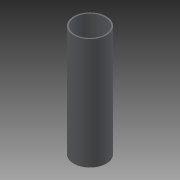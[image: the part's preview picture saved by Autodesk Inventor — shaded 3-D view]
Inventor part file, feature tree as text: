
AUTODESK INVENTOR PART (.ipt)
format: ipt  version: 2014 (Build 180170000, 170)  size: 102,912 bytes
history: native  units: in
note: dims shown in document units (in); Inventor stores cm internally (conversion verified against a paired STEP export)
features: other x14, revolve x1, sketch x1
ambient origin geometry x8: Origin, YZ Plane, XZ Plane, XY Plane, X Axis, Y Axis, Z Axis, Center Point
bodies: Solid1 (feature_tree)
feature tree (16):
  revolve  "Revolution1"  [1 undecoded]
  other  "tube_rear_XY"
  other  "tube_rear_YZ"
  other  "tube_rear_ZX"
  other  "tube_rear_X"
  other  "tube_rear_Y"
  other  "tube_rear_Z"
  other  "tube_rear_Center"
  other  "tube_rod_guide_XY"
  other  "tube_rod_guide_YZ"
  other  "tube_rod_guide_ZX"
  other  "tube_rod_guide_X"
  other  "tube_rod_guide_Y"
  other  "tube_rod_guide_Z"
  other  "tube_rod_guide_Center"
  sketch  "Sketch_4"  dims[d0=360.0deg]
note: 1 required parameter value undecoded (feature->parameter linkage not recoverable at this tier; creation-order binding heuristic only, values carry confidence <= 0.55)
